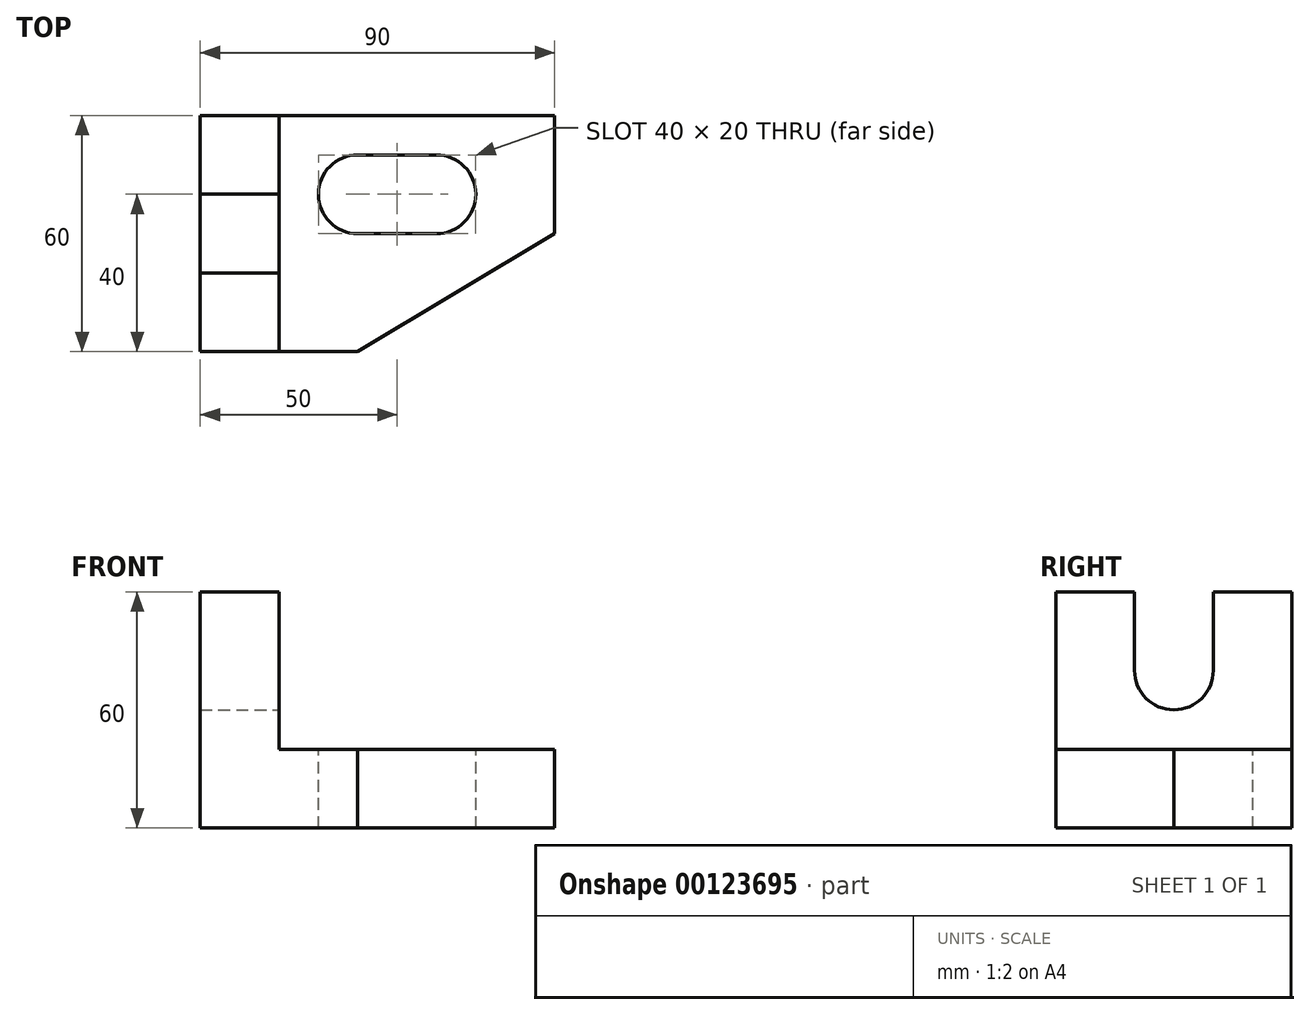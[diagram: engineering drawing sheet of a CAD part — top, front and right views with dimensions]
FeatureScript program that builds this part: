
annotation { "Feature Type Name" : "Feature", "Feature Type Description" : "" }
export const myFeature = defineFeature(function(context is Context, id is Id, definition is map)
    precondition{}
    {
        {
            var Q0;
            Q0=qCreatedBy(makeId("Front.planeOp"),FACE);
            var sketch = newSketch(context, id + "F0", { "sketchPlane" : qUnion([Q0])});
            skLineSegment(sketch, "E0", {"start": v(0, 0) * mm, "end": v(90, 0) * mm});
            skLineSegment(sketch, "E1", {"start": v(90, 0) * mm, "end": v(90, 20) * mm});
            skLineSegment(sketch, "E2", {"start": v(90, 20) * mm, "end": v(20, 20) * mm});
            skLineSegment(sketch, "E3", {"start": v(20, 20) * mm, "end": v(20, 60) * mm});
            skLineSegment(sketch, "E4", {"start": v(20, 60) * mm, "end": v(0, 60) * mm});
            skLineSegment(sketch, "E5", {"start": v(0, 60) * mm, "end": v(0, 0) * mm});
            skSolve(sketch);
        }
        {
            var Q0;
            Q0 = qSketchRegion(id + "F0", true);
            extrude(context, id + "F1", {"entities" : qUnion([Q0]), "depth" : 60 * mm});
        }
        {
            var Q0;
            Q0=makeQuery(id+"F1.opExtrude","SWEPT_FACE",FACE,{"disambiguationData":[OSD([sQuery(id+"F0.wireOp",EDGE,"E3")])]});
            var sketch = newSketch(context, id + "F2", { "sketchPlane" : qUnion([Q0])});
            skLineSegment(sketch, "E6.0", {"start": v(-40, 60) * mm, "end": v(-40, 40) * mm});
            skLineSegment(sketch, "E7.0", {"start": v(-20, 60) * mm, "end": v(-20, 40) * mm});
            skArc(sketch, "E8", {"start": v(-40, 40) * mm, "mid": v(-30, 30) * mm, "end": v(-20, 40) * mm});
            skPoint(sketch, "E9.orphan", {"position": v(-30, 60) * mm});
            skLineSegment(sketch, "E10", {"start": v(-40, 60) * mm, "end": v(-20, 60) * mm});
            skSolve(sketch);
        }
        {
            var Q0;
            Q0=makeQuery(id+"F2.imprint","IMPRINT",FACE,{"disambiguationData":[TD([[makeQuery(id+"F2.imprint","IMPRINT",EDGE,{"derivedFrom":sQuery(id+"F2.wireOp",EDGE,"E6.0")}),1.0]])]});
            extrude(context, id + "F3", {"entities" : qUnion([Q0]), "operationType" : NewBodyOperationType.REMOVE, "endBound" : BoundingType.THROUGH_ALL, "oppositeDirection" : true, "depth" : 25 * mm});
        }
        {
            var Q0;
            Q0=makeQuery(id+"F1.opExtrude","SWEPT_FACE",FACE,{"disambiguationData":[OSD([sQuery(id+"F0.wireOp",EDGE,"E2")])]});
            var sketch = newSketch(context, id + "F4", { "sketchPlane" : qUnion([Q0])});
            skLineSegment(sketch, "E11", {"start": v(90, -30) * mm, "end": v(40, -60) * mm});
            skLineSegment(sketch, "E12", {"start": v(40, -60) * mm, "end": v(90, -60) * mm});
            skLineSegment(sketch, "E13", {"start": v(90, -60) * mm, "end": v(90, -30) * mm});
            skSolve(sketch);
        }
        {
            var Q0;
            Q0=makeQuery(id+"F4.imprint","IMPRINT",FACE,{"disambiguationData":[TD([[makeQuery(id+"F4.imprint","IMPRINT",EDGE,{"derivedFrom":sQuery(id+"F4.wireOp",EDGE,"E11")}),1.0]])]});
            extrude(context, id + "F5", {"entities" : qUnion([Q0]), "operationType" : NewBodyOperationType.REMOVE, "endBound" : BoundingType.THROUGH_ALL, "oppositeDirection" : true, "depth" : 25 * mm});
        }
        {
            var Q0;
            Q0=makeQuery(id+"F1.opExtrude","SWEPT_FACE",FACE,{"disambiguationData":[OSD([sQuery(id+"F0.wireOp",EDGE,"E2")])]});
            var sketch = newSketch(context, id + "F6", { "sketchPlane" : qUnion([Q0])});
            skLineSegment(sketch, "E14", {"start": v(40, -30) * mm, "end": v(60, -30) * mm});
            skLineSegment(sketch, "E15", {"start": v(40, -10) * mm, "end": v(60, -10) * mm});
            skArc(sketch, "E16", {"start": v(40, -10) * mm, "mid": v(30, -20) * mm, "end": v(40, -30) * mm});
            skArc(sketch, "E17", {"start": v(60, -30) * mm, "mid": v(70, -20) * mm, "end": v(60, -10) * mm});
            skSolve(sketch);
        }
        {
            var Q0;
            Q0=makeQuery(id+"F6.imprint","IMPRINT",FACE,{"disambiguationData":[TD([[makeQuery(id+"F6.imprint","IMPRINT",EDGE,{"derivedFrom":sQuery(id+"F6.wireOp",EDGE,"E14")}),1.0]])]});
            extrude(context, id + "F7", {"entities" : qUnion([Q0]), "operationType" : NewBodyOperationType.REMOVE, "endBound" : BoundingType.THROUGH_ALL, "oppositeDirection" : true, "depth" : 25 * mm});
        }
    });
